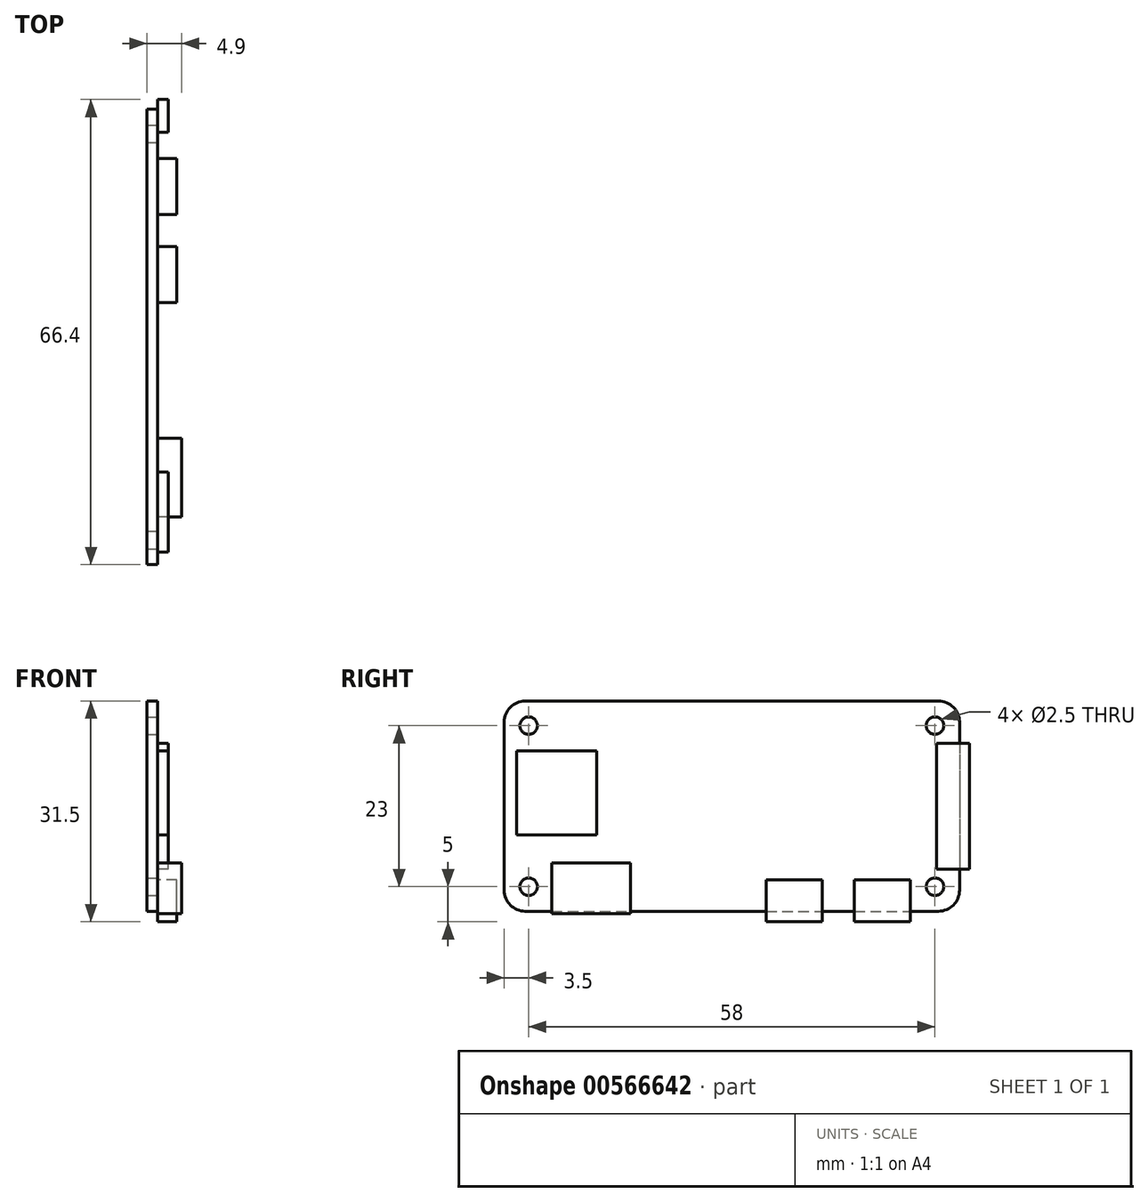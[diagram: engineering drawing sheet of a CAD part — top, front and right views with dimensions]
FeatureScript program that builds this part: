
annotation { "Feature Type Name" : "Feature", "Feature Type Description" : "" }
export const myFeature = defineFeature(function(context is Context, id is Id, definition is map)
    precondition{}
    {
        {
            var Q0;
            Q0=qCreatedBy(makeId("Right.planeOp"),FACE);
            var sketch = newSketch(context, id + "F0", { "sketchPlane" : qUnion([Q0])});
            skLineSegment(sketch, "E0.bottom", {"start": v(-29.5, 15) * mm, "end": v(29.5, 15) * mm});
            skLineSegment(sketch, "E0.top", {"start": v(-29.5, -15) * mm, "end": v(29.5, -15) * mm});
            skLineSegment(sketch, "E0.left", {"start": v(-32.5, 12) * mm, "end": v(-32.5, -12) * mm});
            skLineSegment(sketch, "E0.right", {"start": v(32.5, 12) * mm, "end": v(32.5, -12) * mm});
            skPoint(sketch, "E0.middle", {"position": v(0, 0) * mm});
            skPoint(sketch, "E1.visualSharp", {"position": v(-32.5, 15) * mm});
            skArc(sketch, "E1.filletArc", {"start": v(-29.5, 15) * mm, "mid": v(-31.62, 14.12) * mm, "end": v(-32.5, 12) * mm});
            skPoint(sketch, "E2.visualSharp", {"position": v(-32.5, -15) * mm});
            skArc(sketch, "E2.filletArc", {"start": v(-32.5, -12) * mm, "mid": v(-31.62, -14.12) * mm, "end": v(-29.5, -15) * mm});
            skPoint(sketch, "E3.visualSharp", {"position": v(32.5, -15) * mm});
            skArc(sketch, "E3.filletArc", {"start": v(29.5, -15) * mm, "mid": v(31.62, -14.12) * mm, "end": v(32.5, -12) * mm});
            skPoint(sketch, "E4.visualSharp", {"position": v(32.5, 15) * mm});
            skArc(sketch, "E4.filletArc", {"start": v(32.5, 12) * mm, "mid": v(31.62, 14.12) * mm, "end": v(29.5, 15) * mm});
            skSolve(sketch);
        }
        {
            var Q0;
            Q0=makeQuery(id+"F0.imprint","IMPRINT",FACE,{"disambiguationData":[TD([[makeQuery(id+"F0.imprint","IMPRINT",EDGE,{"derivedFrom":sQuery(id+"F0.wireOp",EDGE,"E0.bottom")}),-1.0]])]});
            extrude(context, id + "F1", {"entities" : qUnion([Q0]), "endBound" : BoundingType.SYMMETRIC, "depth" : 1.5 * mm, "offsetDistance" : 25 * mm});
        }
        {
            var Q0;
            Q0=makeQuery(id+"F1.opExtrude","CAP_FACE",FACE,{"disambiguationData":[OSD([sQuery(id+"F0.wireOp",EDGE,"E0.bottom"),sQuery(id+"F0.wireOp",EDGE,"E0.top"),sQuery(id+"F0.wireOp",EDGE,"E0.left"),sQuery(id+"F0.wireOp",EDGE,"E0.right"),sQuery(id+"F0.wireOp",EDGE,"E1.filletArc"),sQuery(id+"F0.wireOp",EDGE,"E2.filletArc"),sQuery(id+"F0.wireOp",EDGE,"E3.filletArc"),sQuery(id+"F0.wireOp",EDGE,"E4.filletArc")])],"isStart":false});
            var sketch = newSketch(context, id + "F2", { "sketchPlane" : qUnion([Q0])});
            skCircle(sketch, "E5", {"center": v(-29, 11.5) * mm, "radius": 1.25 * mm});
            skCircle(sketch, "E6", {"center": v(29, 11.5) * mm, "radius": 1.25 * mm});
            skCircle(sketch, "E7", {"center": v(29, -11.5) * mm, "radius": 1.25 * mm});
            skCircle(sketch, "E8", {"center": v(-29, -11.5) * mm, "radius": 1.25 * mm});
            skSolve(sketch);
        }
        {
            var Q0;
            Q0=qSketchRegion(id+"F2",true);
            var Q1;
            Q1=makeQuery(id+"F1.opExtrude","CAP_FACE",FACE,{"disambiguationData":[OSD([sQuery(id+"F0.wireOp",EDGE,"E0.bottom"),sQuery(id+"F0.wireOp",EDGE,"E0.top"),sQuery(id+"F0.wireOp",EDGE,"E0.left"),sQuery(id+"F0.wireOp",EDGE,"E0.right"),sQuery(id+"F0.wireOp",EDGE,"E1.filletArc"),sQuery(id+"F0.wireOp",EDGE,"E2.filletArc"),sQuery(id+"F0.wireOp",EDGE,"E3.filletArc"),sQuery(id+"F0.wireOp",EDGE,"E4.filletArc")])],"isStart":true});
            extrude(context, id + "F3", {"entities" : qUnion([Q0]), "operationType" : NewBodyOperationType.REMOVE, "endBound" : BoundingType.UP_TO_SURFACE, "oppositeDirection" : true, "depth" : 25 * mm, "endBoundEntityFace" : qUnion([Q1]), "offsetDistance" : 25 * mm});
        }
        {
            var Q0;
            Q0=makeQuery(id+"F1.opExtrude","CAP_FACE",FACE,{"disambiguationData":[OSD([sQuery(id+"F0.wireOp",EDGE,"E0.bottom"),sQuery(id+"F0.wireOp",EDGE,"E0.top"),sQuery(id+"F0.wireOp",EDGE,"E0.left"),sQuery(id+"F0.wireOp",EDGE,"E0.right"),sQuery(id+"F0.wireOp",EDGE,"E1.filletArc"),sQuery(id+"F0.wireOp",EDGE,"E2.filletArc"),sQuery(id+"F0.wireOp",EDGE,"E3.filletArc"),sQuery(id+"F0.wireOp",EDGE,"E4.filletArc")])],"isStart":false});
            var sketch = newSketch(context, id + "F4", { "sketchPlane" : qUnion([Q0])});
            skLineSegment(sketch, "E9.bottom", {"start": v(-14.47, -15.35) * mm, "end": v(-25.72, -15.35) * mm});
            skLineSegment(sketch, "E9.top", {"start": v(-14.48, -8.1) * mm, "end": v(-25.73, -8.1) * mm});
            skLineSegment(sketch, "E9.left", {"start": v(-14.47, -15.35) * mm, "end": v(-14.48, -8.1) * mm});
            skLineSegment(sketch, "E9.right", {"start": v(-25.73, -15.35) * mm, "end": v(-25.73, -8.1) * mm});
            skPoint(sketch, "E9.middle", {"position": v(-20.1, -11.72) * mm});
            skLineSegment(sketch, "E10.bottom", {"start": v(12.9, -16.5) * mm, "end": v(4.9, -16.5) * mm});
            skLineSegment(sketch, "E10.top", {"start": v(12.9, -10.5) * mm, "end": v(4.9, -10.5) * mm});
            skLineSegment(sketch, "E10.left", {"start": v(12.9, -16.5) * mm, "end": v(12.9, -10.5) * mm});
            skLineSegment(sketch, "E10.right", {"start": v(4.9, -16.5) * mm, "end": v(4.9, -10.5) * mm});
            skPoint(sketch, "E10.middle", {"position": v(8.9, -13.5) * mm});
            skLineSegment(sketch, "E11.bottom", {"start": v(17.5, -10.5) * mm, "end": v(25.5, -10.5) * mm});
            skLineSegment(sketch, "E11.top", {"start": v(17.5, -16.5) * mm, "end": v(25.5, -16.5) * mm});
            skLineSegment(sketch, "E11.left", {"start": v(17.5, -10.5) * mm, "end": v(17.5, -16.5) * mm});
            skLineSegment(sketch, "E11.right", {"start": v(25.5, -10.5) * mm, "end": v(25.5, -16.5) * mm});
            skPoint(sketch, "E11.middle", {"position": v(21.5, -13.5) * mm});
            skLineSegment(sketch, "E12.bottom", {"start": v(33.9, -9) * mm, "end": v(29.2, -9) * mm});
            skLineSegment(sketch, "E12.top", {"start": v(33.9, 9) * mm, "end": v(29.2, 9) * mm});
            skLineSegment(sketch, "E12.left", {"start": v(33.9, -9) * mm, "end": v(33.9, 9) * mm});
            skLineSegment(sketch, "E12.right", {"start": v(29.2, -9) * mm, "end": v(29.2, 9) * mm});
            skPoint(sketch, "E12.middle", {"position": v(31.55, 0) * mm});
            skLineSegment(sketch, "E13.bottom", {"start": v(-30.7, 7.9) * mm, "end": v(-19.3, 7.9) * mm});
            skLineSegment(sketch, "E13.top", {"start": v(-30.7, -4.1) * mm, "end": v(-19.3, -4.1) * mm});
            skLineSegment(sketch, "E13.left", {"start": v(-30.7, 7.9) * mm, "end": v(-30.7, -4.1) * mm});
            skLineSegment(sketch, "E13.right", {"start": v(-19.3, 7.9) * mm, "end": v(-19.3, -4.1) * mm});
            skPoint(sketch, "E13.middle", {"position": v(-25, 1.9) * mm});
            skSolve(sketch);
        }
        {
            var Q0;
            {var subQ0=sQuery(id+"F4.wireOp",EDGE,"E9.bottom");Q0=makeQuery(id+"F4.imprint","IMPRINT",FACE,{"disambiguationData":[TD([[makeQuery(id+"F4.imprint","IMPRINT",EDGE,{"derivedFrom":subQ0}),-1.0]])]});}
            var Q1;
            {var subQ0=sQuery(id+"F4.wireOp",EDGE,"E9.top");Q1=makeQuery(id+"F4.imprint","IMPRINT",FACE,{"disambiguationData":[TD([[makeQuery(id+"F4.imprint","IMPRINT",EDGE,{"derivedFrom":subQ0}),1.0]])]});}
            extrude(context, id + "F5", {"entities" : qUnion([Q0, Q1]), "operationType" : NewBodyOperationType.ADD, "depth" : 3.4 * mm, "offsetDistance" : 25 * mm});
        }
        {
            var Q0;
            {var subQ0=sQuery(id+"F4.wireOp",EDGE,"E10.top");Q0=makeQuery(id+"F4.imprint","IMPRINT",FACE,{"disambiguationData":[TD([[makeQuery(id+"F4.imprint","IMPRINT",EDGE,{"derivedFrom":subQ0}),1.0]])]});}
            var Q1;
            {var subQ0=sQuery(id+"F4.wireOp",EDGE,"E10.bottom");Q1=makeQuery(id+"F4.imprint","IMPRINT",FACE,{"disambiguationData":[TD([[makeQuery(id+"F4.imprint","IMPRINT",EDGE,{"derivedFrom":subQ0}),-1.0]])]});}
            var Q2;
            {var subQ0=sQuery(id+"F4.wireOp",EDGE,"E11.bottom");Q2=makeQuery(id+"F4.imprint","IMPRINT",FACE,{"disambiguationData":[TD([[makeQuery(id+"F4.imprint","IMPRINT",EDGE,{"derivedFrom":subQ0}),-1.0]])]});}
            var Q3;
            {var subQ0=sQuery(id+"F4.wireOp",EDGE,"E11.top");Q3=makeQuery(id+"F4.imprint","IMPRINT",FACE,{"disambiguationData":[TD([[makeQuery(id+"F4.imprint","IMPRINT",EDGE,{"derivedFrom":subQ0}),1.0]])]});}
            extrude(context, id + "F6", {"entities" : qUnion([Q0, Q1, Q2, Q3]), "operationType" : NewBodyOperationType.ADD, "depth" : 2.75 * mm, "offsetDistance" : 25 * mm});
        }
        {
            var Q0;
            {var subQ0=sQuery(id+"F4.wireOp",EDGE,"E12.left");Q0=makeQuery(id+"F4.imprint","IMPRINT",FACE,{"disambiguationData":[TD([[makeQuery(id+"F4.imprint","IMPRINT",EDGE,{"derivedFrom":subQ0}),1.0]])]});}
            var Q1;
            {var subQ0=sQuery(id+"F4.wireOp",EDGE,"E12.right");Q1=makeQuery(id+"F4.imprint","IMPRINT",FACE,{"disambiguationData":[TD([[makeQuery(id+"F4.imprint","IMPRINT",EDGE,{"derivedFrom":subQ0}),-1.0]])]});}
            extrude(context, id + "F7", {"entities" : qUnion([Q0, Q1]), "operationType" : NewBodyOperationType.ADD, "depth" : 1.5 * mm, "offsetDistance" : 25 * mm});
        }
        {
            var Q0;
            Q0=makeQuery(id+"F4.imprint","IMPRINT",FACE,{"disambiguationData":[TD([[makeQuery(id+"F4.imprint","IMPRINT",EDGE,{"derivedFrom":sQuery(id+"F4.wireOp",EDGE,"E13.bottom")}),-1.0]])]});
            extrude(context, id + "F8", {"entities" : qUnion([Q0]), "operationType" : NewBodyOperationType.ADD, "depth" : 1.5 * mm, "offsetDistance" : 25 * mm});
        }
    });
